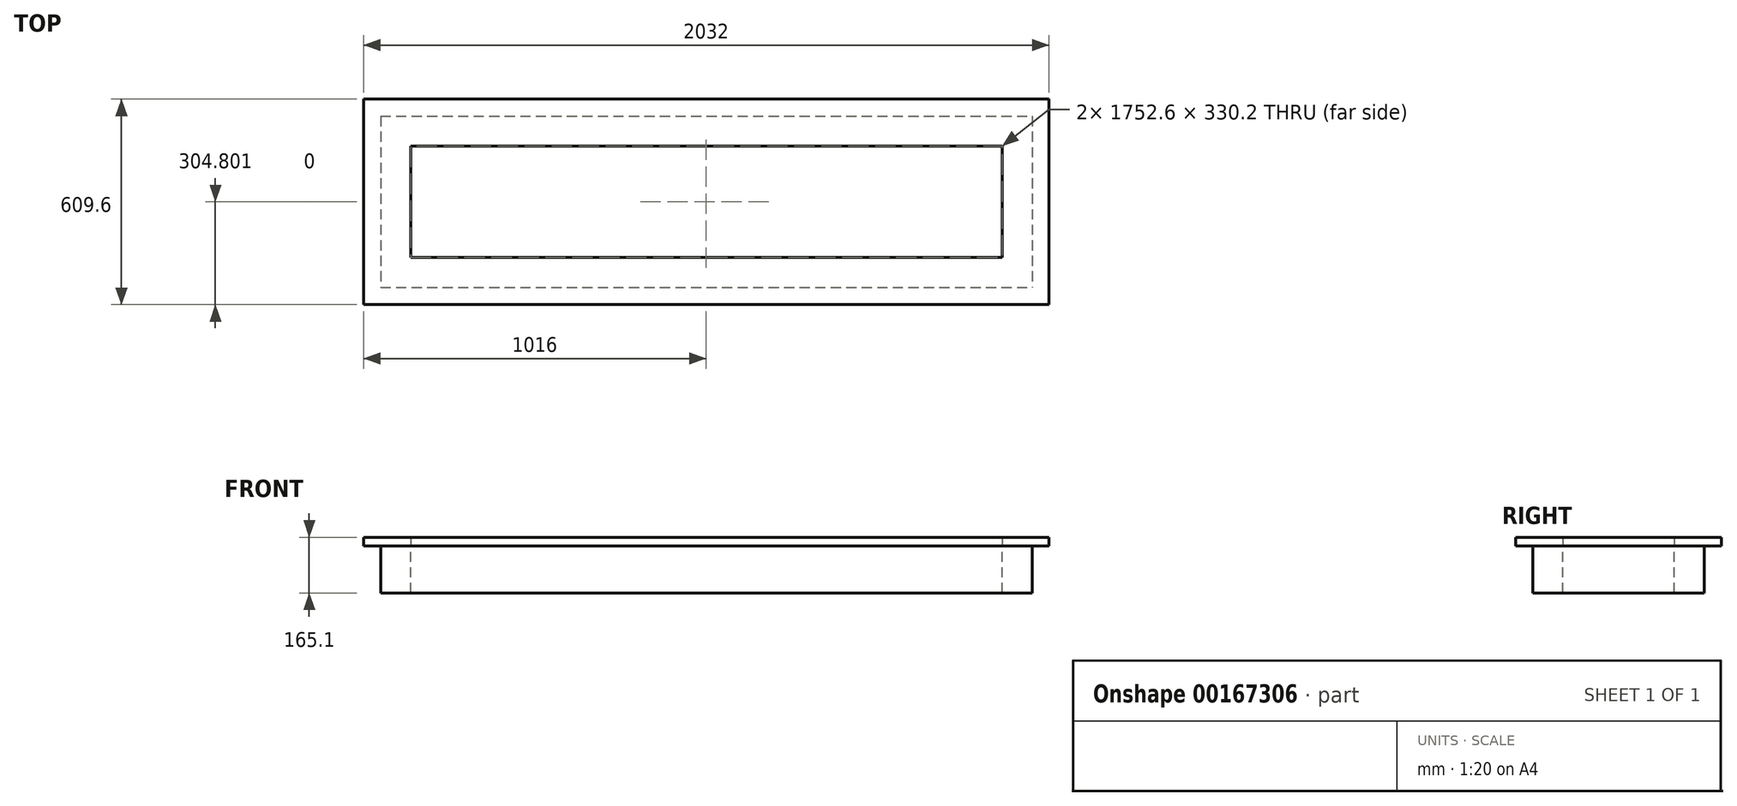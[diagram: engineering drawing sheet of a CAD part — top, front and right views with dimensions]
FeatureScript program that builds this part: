
annotation { "Feature Type Name" : "Feature", "Feature Type Description" : "" }
export const myFeature = defineFeature(function(context is Context, id is Id, definition is map)
    precondition{}
    {
        {
            var Q0;
            Q0=qCreatedBy(makeId("Top.planeOp"),FACE);
            var sketch = newSketch(context, id + "F0", { "sketchPlane" : qUnion([Q0])});
            skLineSegment(sketch, "E0.bottom", {"start": v(-1034.3, 355.83) * mm, "end": v(997.7, 355.83) * mm});
            skLineSegment(sketch, "E0.top", {"start": v(-1034.3, -253.77) * mm, "end": v(997.7, -253.77) * mm});
            skLineSegment(sketch, "E0.left", {"start": v(-1034.3, 355.83) * mm, "end": v(-1034.3, -253.77) * mm});
            skLineSegment(sketch, "E0.right", {"start": v(997.7, 355.83) * mm, "end": v(997.7, -253.77) * mm});
            skLineSegment(sketch, "E1.0", {"start": v(-894.6, 216.13) * mm, "end": v(858, 216.13) * mm});
            skLineSegment(sketch, "E2.0", {"start": v(858, 216.13) * mm, "end": v(858, -114.07) * mm});
            skLineSegment(sketch, "E3.0", {"start": v(-983.5, -202.97) * mm, "end": v(946.9, -202.97) * mm});
            skLineSegment(sketch, "E4.0", {"start": v(946.9, 305.03) * mm, "end": v(946.9, -202.97) * mm});
            skLineSegment(sketch, "E5.0", {"start": v(-983.5, 305.03) * mm, "end": v(946.9, 305.03) * mm});
            skLineSegment(sketch, "E6.0", {"start": v(-983.5, 305.03) * mm, "end": v(-983.5, -202.97) * mm});
            skLineSegment(sketch, "E7", {"start": v(-1034.3, -253.77) * mm, "end": v(-894.6, -114.07) * mm});
            skLineSegment(sketch, "E8", {"start": v(-1034.3, 355.83) * mm, "end": v(-894.6, 216.13) * mm});
            skLineSegment(sketch, "E9", {"start": v(858, 216.13) * mm, "end": v(997.7, 355.83) * mm});
            skLineSegment(sketch, "E10", {"start": v(858, -114.07) * mm, "end": v(997.7, -253.77) * mm});
            skLineSegment(sketch, "E11.trimOffspring", {"start": v(-894.6, -114.07) * mm, "end": v(858, -114.07) * mm});
            skLineSegment(sketch, "E12.trimOffspring", {"start": v(-894.6, 216.13) * mm, "end": v(-894.6, -114.07) * mm});
            skSolve(sketch);
        }
        {
            var Q0;
            Q0 = qSketchRegion(id + "F0", true);
            var Q1;
            {var subQ0=sQuery(id+"F0.wireOp",EDGE,"E6.0");Q1=makeQuery(id+"F0.imprint","IMPRINT",FACE,{"disambiguationData":[TD([[makeQuery(id+"F0.imprint","IMPRINT",EDGE,{"derivedFrom":subQ0}),1.0]])]});}
            var Q2;
            {var subQ0=sQuery(id+"F0.wireOp",EDGE,"E1.0");Q2=makeQuery(id+"F0.imprint","IMPRINT",FACE,{"disambiguationData":[TD([[makeQuery(id+"F0.imprint","IMPRINT",EDGE,{"derivedFrom":subQ0}),1.0]])]});}
            var Q3;
            {var subQ0=sQuery(id+"F0.wireOp",EDGE,"E2.0");Q3=makeQuery(id+"F0.imprint","IMPRINT",FACE,{"disambiguationData":[TD([[makeQuery(id+"F0.imprint","IMPRINT",EDGE,{"derivedFrom":subQ0}),1.0]])]});}
            var Q4;
            {var subQ0=sQuery(id+"F0.wireOp",EDGE,"E3.0");Q4=makeQuery(id+"F0.imprint","IMPRINT",FACE,{"disambiguationData":[TD([[makeQuery(id+"F0.imprint","IMPRINT",EDGE,{"derivedFrom":subQ0}),1.0]])]});}
            extrude(context, id + "F1", {"entities" : qUnion([Q0, Q1, Q2, Q3, Q4]), "depth" : 25.4 * mm});
        }
        {
            var Q0;
            {var subQ0=sQuery(id+"F0.wireOp",EDGE,"E6.0");Q0=makeQuery(id+"F0.imprint","IMPRINT",FACE,{"disambiguationData":[TD([[makeQuery(id+"F0.imprint","IMPRINT",EDGE,{"derivedFrom":subQ0}),1.0]])]});}
            var Q1;
            {var subQ0=sQuery(id+"F0.wireOp",EDGE,"E3.0");Q1=makeQuery(id+"F0.imprint","IMPRINT",FACE,{"disambiguationData":[TD([[makeQuery(id+"F0.imprint","IMPRINT",EDGE,{"derivedFrom":subQ0}),1.0]])]});}
            var Q2;
            {var subQ0=sQuery(id+"F0.wireOp",EDGE,"E2.0");Q2=makeQuery(id+"F0.imprint","IMPRINT",FACE,{"disambiguationData":[TD([[makeQuery(id+"F0.imprint","IMPRINT",EDGE,{"derivedFrom":subQ0}),1.0]])]});}
            var Q3;
            {var subQ0=sQuery(id+"F0.wireOp",EDGE,"E1.0");Q3=makeQuery(id+"F0.imprint","IMPRINT",FACE,{"disambiguationData":[TD([[makeQuery(id+"F0.imprint","IMPRINT",EDGE,{"derivedFrom":subQ0}),1.0]])]});}
            var Q4;
            Q4=sQuery(id+"F0.wireOp",EDGE,"E6.0");
            var Q5;
            Q5=sQuery(id+"F0.wireOp",EDGE,"E3.0");
            var Q6;
            Q6=sQuery(id+"F0.wireOp",EDGE,"E12.trimOffspring");
            var Q7;
            Q7=sQuery(id+"F0.wireOp",EDGE,"E4.0");
            var Q8;
            Q8=sQuery(id+"F0.wireOp",EDGE,"E5.0");
            var Q9;
            Q9=sQuery(id+"F0.wireOp",EDGE,"E1.0");
            var Q10;
            Q10=sQuery(id+"F0.wireOp",EDGE,"E2.0");
            var Q11;
            Q11=sQuery(id+"F0.wireOp",EDGE,"E11.trimOffspring");
            extrude(context, id + "F2", {"entities" : qUnion([Q0, Q1, Q2, Q3]), "surfaceEntities" : qUnion([Q4, Q5, Q6, Q7, Q8, Q9, Q10, Q11]), "oppositeDirection" : true, "depth" : 139.7 * mm});
        }
    });
